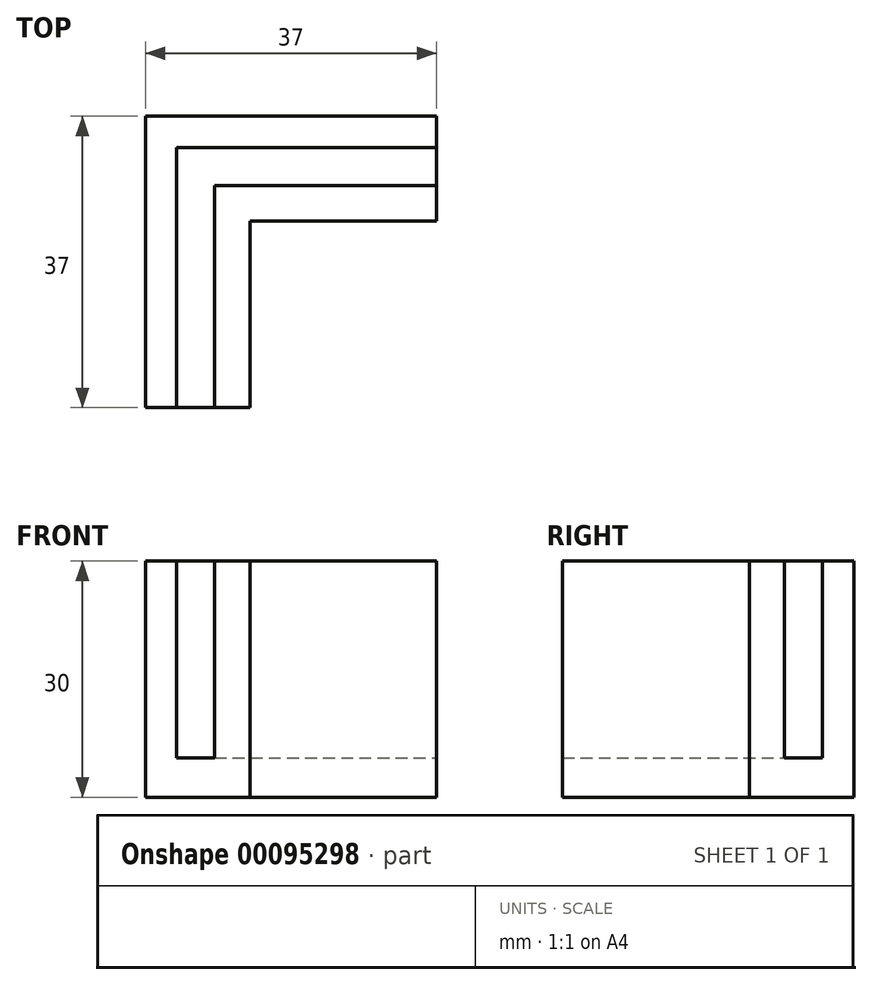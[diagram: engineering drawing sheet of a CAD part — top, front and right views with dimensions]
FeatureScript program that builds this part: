
annotation { "Feature Type Name" : "Feature", "Feature Type Description" : "" }
export const myFeature = defineFeature(function(context is Context, id is Id, definition is map)
    precondition{}
    {
        {
            var Q0;
            Q0=qCreatedBy(makeId("Top.planeOp"),FACE);
            var sketch = newSketch(context, id + "F0", { "sketchPlane" : qUnion([Q0])});
            skLineSegment(sketch, "E0", {"start": v(-13.28, -23.72) * mm, "end": v(-13.28, 13.28) * mm});
            skLineSegment(sketch, "E1", {"start": v(-13.28, 13.28) * mm, "end": v(23.72, 13.28) * mm});
            skLineSegment(sketch, "E2", {"start": v(23.72, 13.28) * mm, "end": v(23.72, 0) * mm});
            skLineSegment(sketch, "E3", {"start": v(23.72, 0) * mm, "end": v(0, 0) * mm});
            skLineSegment(sketch, "E4", {"start": v(0, 0) * mm, "end": v(0, -23.72) * mm});
            skLineSegment(sketch, "E5", {"start": v(0, -23.72) * mm, "end": v(-13.28, -23.72) * mm});
            skSolve(sketch);
        }
        {
            var Q0;
            Q0=makeQuery(id+"F0.imprint","IMPRINT",FACE,{"disambiguationData":[TD([[makeQuery(id+"F0.imprint","IMPRINT",EDGE,{"derivedFrom":sQuery(id+"F0.wireOp",EDGE,"E0")}),-1.0]])]});
            extrude(context, id + "F1", {"entities" : qUnion([Q0]), "depth" : 30 * mm});
        }
        {
            var Q0;
            Q0=makeQuery(id+"F1.opExtrude","CAP_FACE",FACE,{"disambiguationData":[OSD([sQuery(id+"F0.wireOp",EDGE,"E0"),sQuery(id+"F0.wireOp",EDGE,"E1"),sQuery(id+"F0.wireOp",EDGE,"E2"),sQuery(id+"F0.wireOp",EDGE,"E3"),sQuery(id+"F0.wireOp",EDGE,"E4"),sQuery(id+"F0.wireOp",EDGE,"E5")])],"isStart":false});
            var sketch = newSketch(context, id + "F2", { "sketchPlane" : qUnion([Q0])});
            skLineSegment(sketch, "E6", {"start": v(-9.28, -23.72) * mm, "end": v(-9.28, 9.28) * mm});
            skLineSegment(sketch, "E7", {"start": v(-9.28, 9.28) * mm, "end": v(23.72, 9.28) * mm});
            skLineSegment(sketch, "E8", {"start": v(-4.48, -23.72) * mm, "end": v(-4.48, 4.48) * mm});
            skLineSegment(sketch, "E9", {"start": v(-4.48, 4.48) * mm, "end": v(23.72, 4.48) * mm});
            skSolve(sketch);
        }
        {
            var Q0;
            {var subQ3=sQuery(id+"F2.wireOp",EDGE,"E6");Q0=makeQuery(id+"F2.imprint","IMPRINT",FACE,{"disambiguationData":[TD([[makeQuery(id+"F2.imprint","IMPRINT",EDGE,{"derivedFrom":subQ3}),-1.0]])]});}
            extrude(context, id + "F3", {"entities" : qUnion([Q0]), "operationType" : NewBodyOperationType.REMOVE, "oppositeDirection" : true, "depth" : 25 * mm});
        }
    });
